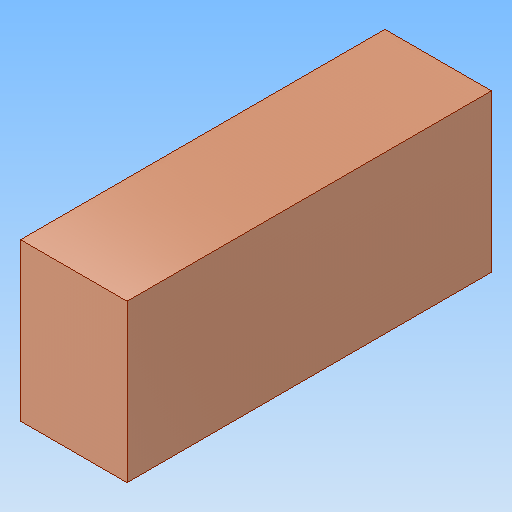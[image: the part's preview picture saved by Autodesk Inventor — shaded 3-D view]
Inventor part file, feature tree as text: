
AUTODESK INVENTOR PART (.ipt)
format: ipt  version: 2019 (Build 230136000, 136)  size: 124,928 bytes
history: native  units: mm
features: other x1, extrude x1, sketch x1
ambient origin geometry x8: Origin, YZ Plane, XZ Plane, XY Plane, X Axis, Y Axis, Z Axis, Center Point
bodies: Body1 (feature_tree)
feature tree (3):
  other  "Твердое тело1"
  extrude  "Выдавливание1"  Depth=29311.5mm TaperAngle=0.0deg
  sketch  "Эскиз1"
